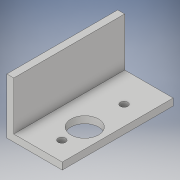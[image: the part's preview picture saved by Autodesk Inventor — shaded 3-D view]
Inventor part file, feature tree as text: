
AUTODESK INVENTOR PART (.ipt)
format: ipt  version: 2018 (Build 220112000, 112)  size: 119,296 bytes
history: native  units: in
note: dims shown in document units (in); Inventor stores cm internally (conversion verified against a paired STEP export)
features: extrude x3, sketch x3
ambient origin geometry x8: Origin, YZ Plane, XZ Plane, XY Plane, X Axis, Y Axis, Z Axis, Center Point
bodies: Solid1 (feature_tree)
feature tree (6):
  extrude  "Extrusion1"  Depth=1.0in
  extrude  "Extrusion2"  Depth=0.125in
  extrude  "Extrusion3"  Depth=2.0in
  sketch  "Sketch1"  dims[d0=0.125in d1=1.0in]
  sketch  "Sketch2"  dims[d2=1.0in d3=0.125in]
  sketch  "Sketch3"  dims[d4=2.0in d5=0.0in d6=0.655in d7=0.75in d8=90.0deg d9=0.5in d10=2.0in d11=0.0in d12=0.413in d13=1.122in d14=0.134in d15=0.134in d16=2.0in d17=0.0in]
